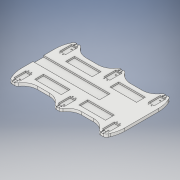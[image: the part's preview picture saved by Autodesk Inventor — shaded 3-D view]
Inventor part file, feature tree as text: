
AUTODESK INVENTOR PART (.ipt)
format: ipt  version: 2017 (Build 210142000, 142)  size: 404,992 bytes
history: native  units: mm
features: extrude x7, sketch x7, fillet x3
ambient origin geometry x8: Origin, YZ Plane, XZ Plane, XY Plane, X Axis, Y Axis, Z Axis, Center Point
bodies: Solid1 (feature_tree)
feature tree (17):
  extrude  "Extrusion1"  Depth=30.0mm
  extrude  "Extrusion2"  Depth=10.0mm
  extrude  "Extrusion3"  Depth=10.0mm
  fillet  "Fillet1"  [1 undecoded]
  fillet  "Fillet2"  Radius=11.5mm
  fillet  "Fillet3"  Radius=5.0mm
  extrude  "Extrusion10"  Depth=40.5mm
  extrude  "Extrusion11"  Depth=5.0mm
  extrude  "Extrusion12"  TaperAngle=0.0deg  [1 undecoded]
  extrude  "Extrusion13"  Depth=5.0mm
  sketch  "Sketch1"  dims[d0=30.0mm d1=82.5mm]
  sketch  "Sketch2"  dims[d2=26.75mm d3=10.0mm]
  sketch  "Sketch3"  dims[d4=120.0mm d5=10.0mm d6=0.0mm d7=11.5mm d8=5.0mm]
  sketch  "Sketch10"  dims[d9=20.0mm d10=40.5mm]
  sketch  "Sketch11"  dims[d11=5.0mm d12=5.0mm]
  sketch  "Sketch12"  dims[d13=5.0mm d14=0.0mm]
  sketch  "Sketch13"  dims[d17=4.0mm d18=4.0mm d19=4.5mm d25=2.75mm d26=2.75mm d27=2.75mm d28=5.0mm d29=0.0mm d37=10.0mm d38=50.0mm d69=100.0mm d70=3.0mm d75=10.0mm d76=4.0mm d77=10.0mm d78=0.0mm d81=7.5mm d82=2.0mm d83=0.0mm d84=36.0mm d85=50.0mm d86=5.0mm d87=0.0mm d88=90.0mm d89=30.0mm d90=15.0mm d91=15.0mm d92=5.0mm d93=0.0mm]
note: 2 required parameter values undecoded (feature->parameter linkage not recoverable at this tier; creation-order binding heuristic only, values carry confidence <= 0.55)
